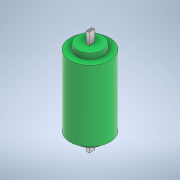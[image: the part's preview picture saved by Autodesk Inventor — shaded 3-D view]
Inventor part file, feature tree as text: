
AUTODESK INVENTOR PART (.ipt)
format: ipt  version: 2021 (Build 250183000, 183)  size: 138,240 bytes
history: native  units: mm
features: extrude x5, sketch x5
ambient origin geometry x8: Origin, YZ Plane, XZ Plane, XY Plane, X Axis, Y Axis, Z Axis, Center Point
bodies: Solid1 (feature_tree)
feature tree (10):
  extrude  "Extrusion1"  Depth=25.0mm TaperAngle=0.0deg
  sketch  "Sketch2"  dims[d3=9.0mm d4=9.0mm]
  extrude  "Extrusion2"  Depth=9.0mm
  extrude  "Extrusion3"  Depth=2.0mm TaperAngle=0.0deg
  extrude  "Extrusion4"  Depth=2.0mm
  extrude  "Extrusion5"  Depth=4.0mm TaperAngle=0.0deg
  sketch  "Sketch1"  dims[d0=14.0mm d1=25.0mm d2=0.0mm]
  sketch  "Sketch3"  dims[d5=4.0mm d6=0.0mm d7=2.0mm d8=0.0mm]
  sketch  "Sketch4"  dims[d9=1.0mm d10=2.0mm]
  sketch  "Sketch5"  dims[d11=4.0mm d12=0.0mm d13=4.0mm d14=0.0mm]
